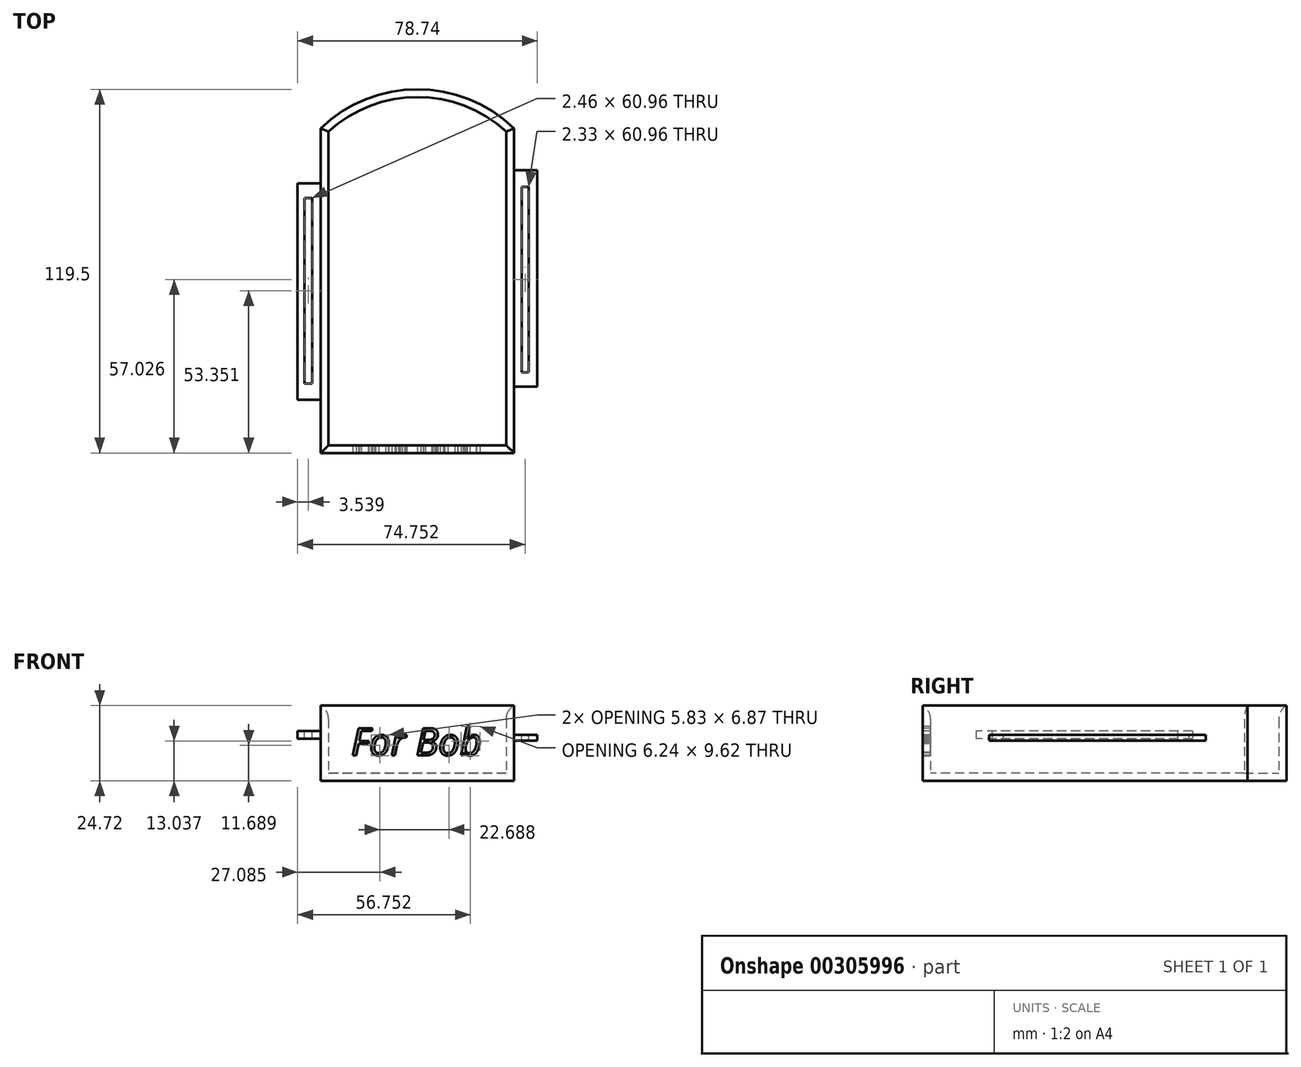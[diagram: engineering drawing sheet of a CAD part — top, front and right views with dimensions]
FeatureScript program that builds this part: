
annotation { "Feature Type Name" : "Feature", "Feature Type Description" : "" }
export const myFeature = defineFeature(function(context is Context, id is Id, definition is map)
    precondition{}
    {
        {
            var Q0;
            Q0=qCreatedBy(makeId("Top.planeOp"),FACE);
            var sketch = newSketch(context, id + "F0", { "sketchPlane" : qUnion([Q0])});
            skLineSegment(sketch, "E0", {"start": v(-35.9, 50.46) * mm, "end": v(-35.9, -56.22) * mm});
            skLineSegment(sketch, "E1", {"start": v(-35.9, -56.22) * mm, "end": v(27.6, -56.22) * mm});
            skLineSegment(sketch, "E2", {"start": v(27.6, -56.22) * mm, "end": v(27.6, 50.46) * mm});
            skArc(sketch, "E3", {"start": v(27.6, 50.46) * mm, "mid": v(-4.14, 63.28) * mm, "end": v(-35.9, 50.46) * mm});
            skSolve(sketch);
        }
        {
            var Q0;
            Q0 = qSketchRegion(id + "F0", true);
            extrude(context, id + "F1", {"entities" : qUnion([Q0]), "depth" : 25.4 * mm});
        }
        {
            var Q0;
            Q0=makeQuery(id+"F1.opExtrude","CAP_FACE",FACE,{"disambiguationData":[OSD([sQuery(id+"F0.wireOp",EDGE,"E0"),sQuery(id+"F0.wireOp",EDGE,"E1"),sQuery(id+"F0.wireOp",EDGE,"E2"),sQuery(id+"F0.wireOp",EDGE,"E3")])],"isStart":false});
            shell(context, id + "F2", {"entities" : qUnion([Q0]), "thickness" : 2.54 * mm});
        }
        {
            var Q0;
            {var subQ0=sQuery(id+"F0.wireOp",EDGE,"E3");Q0=makeQuery(id+"F2.opShell","OFFSET_EDGE",EDGE,{"disambiguationData":[OSD([subQ0]),TDD([makeQuery(id+"F1.opExtrude","CAP_EDGE",EDGE,{"disambiguationData":[OSD([subQ0])],"isStart":false})])]});}
            var Q1;
            {var subQ0=sQuery(id+"F0.wireOp",EDGE,"E0");Q1=makeQuery(id+"F2.opShell","OFFSET_EDGE",EDGE,{"disambiguationData":[OSD([subQ0]),TDD([makeQuery(id+"F1.opExtrude","CAP_EDGE",EDGE,{"disambiguationData":[OSD([subQ0])],"isStart":false})])]});}
            var Q2;
            {var subQ0=sQuery(id+"F0.wireOp",EDGE,"E2");Q2=makeQuery(id+"F2.opShell","OFFSET_EDGE",EDGE,{"disambiguationData":[OSD([subQ0]),TDD([makeQuery(id+"F1.opExtrude","CAP_EDGE",EDGE,{"disambiguationData":[OSD([subQ0])],"isStart":false})])]});}
            var Q3;
            {var subQ0=sQuery(id+"F0.wireOp",EDGE,"E1");Q3=makeQuery(id+"F2.opShell","OFFSET_EDGE",EDGE,{"disambiguationData":[OSD([subQ0]),TDD([makeQuery(id+"F1.opExtrude","CAP_EDGE",EDGE,{"disambiguationData":[OSD([subQ0])],"isStart":false})])]});}
            fillet(context, id + "F3", {"entities" : qUnion([Q0, Q1, Q2, Q3]), "radius" : 5.08 * mm, "tangentPropagation" : true, "allowEdgeOverflow" : false});
        }
        {
            var Q0;
            Q0=makeQuery(id+"F1.opExtrude","SWEPT_FACE",FACE,{"disambiguationData":[OSD([sQuery(id+"F0.wireOp",EDGE,"E1")])]});
            var sketch = newSketch(context, id + "F4", { "sketchPlane" : qUnion([Q0])});
            skText(sketch, "E4", { "text": "For Bob", "fontName": "OpenSans-Italic.ttf"});
            const initialGuessF4  = {"E4": [-0.02584, 0.00835, 1, 0, 0.009]};
            skSetInitialGuess(sketch, initialGuessF4);
            skSolve(sketch);
        }
        {
            var Q0;
            Q0 = qSketchRegion(id + "F4", true);
            extrude(context, id + "F5", {"entities" : qUnion([Q0]), "operationType" : NewBodyOperationType.REMOVE, "oppositeDirection" : true, "depth" : 12.7 * mm});
        }
        {
            var Q0;
            Q0=makeQuery(id+"F1.opExtrude","SWEPT_FACE",FACE,{"disambiguationData":[OSD([sQuery(id+"F0.wireOp",EDGE,"E2")])]});
            var sketch = newSketch(context, id + "F6", { "sketchPlane" : qUnion([Q0])});
            skLineSegment(sketch, "E5.bottom", {"start": v(-34.4, 15.16) * mm, "end": v(36.73, 15.16) * mm});
            skLineSegment(sketch, "E5.top", {"start": v(-34.4, 13.18) * mm, "end": v(36.73, 13.18) * mm});
            skLineSegment(sketch, "E5.left", {"start": v(-34.4, 15.16) * mm, "end": v(-34.4, 13.18) * mm});
            skLineSegment(sketch, "E5.right", {"start": v(36.73, 15.16) * mm, "end": v(36.73, 13.18) * mm});
            skSolve(sketch);
        }
        {
            var Q0;
            Q0 = qSketchRegion(id + "F6", true);
            extrude(context, id + "F7", {"entities" : qUnion([Q0]), "operationType" : NewBodyOperationType.ADD, "depth" : 7.62 * mm});
        }
        {
            var Q0;
            Q0=makeQuery(id+"F7.opExtrude","SWEPT_FACE",FACE,{"disambiguationData":[OSD([sQuery(id+"F6.wireOp",EDGE,"E5.bottom")])]});
            var sketch = newSketch(context, id + "F8", { "sketchPlane" : qUnion([Q0])});
            skLineSegment(sketch, "E6.bottom", {"start": v(30.08, -29.67) * mm, "end": v(32.4, -29.67) * mm});
            skLineSegment(sketch, "E6.top", {"start": v(30.08, 31.29) * mm, "end": v(32.4, 31.29) * mm});
            skLineSegment(sketch, "E6.left", {"start": v(30.08, -29.67) * mm, "end": v(30.08, 31.29) * mm});
            skLineSegment(sketch, "E6.right", {"start": v(32.4, -29.67) * mm, "end": v(32.4, 31.29) * mm});
            skSolve(sketch);
        }
        {
            var Q0;
            Q0 = qSketchRegion(id + "F8", true);
            extrude(context, id + "F9", {"entities" : qUnion([Q0]), "operationType" : NewBodyOperationType.REMOVE, "oppositeDirection" : true, "depth" : 25.4 * mm});
        }
        {
            var Q0;
            Q0=makeQuery(id+"F1.opExtrude","SWEPT_FACE",FACE,{"disambiguationData":[OSD([sQuery(id+"F0.wireOp",EDGE,"E0")])]});
            var sketch = newSketch(context, id + "F10", { "sketchPlane" : qUnion([Q0])});
            skLineSegment(sketch, "E7.bottom", {"start": v(-32.36, 16.41) * mm, "end": v(38.76, 16.41) * mm});
            skLineSegment(sketch, "E7.top", {"start": v(-32.36, 13.81) * mm, "end": v(38.76, 13.81) * mm});
            skLineSegment(sketch, "E7.left", {"start": v(-32.36, 16.41) * mm, "end": v(-32.36, 13.81) * mm});
            skLineSegment(sketch, "E7.right", {"start": v(38.76, 16.41) * mm, "end": v(38.76, 13.81) * mm});
            skSolve(sketch);
        }
        {
            var Q0;
            Q0 = qSketchRegion(id + "F10", true);
            extrude(context, id + "F11", {"entities" : qUnion([Q0]), "operationType" : NewBodyOperationType.ADD, "depth" : 7.62 * mm});
        }
        {
            var Q0;
            Q0=makeQuery(id+"F11.opExtrude","SWEPT_FACE",FACE,{"disambiguationData":[OSD([sQuery(id+"F10.wireOp",EDGE,"E7.bottom")])]});
            var sketch = newSketch(context, id + "F12", { "sketchPlane" : qUnion([Q0])});
            skLineSegment(sketch, "E8.bottom", {"start": v(-38.74, 27.61) * mm, "end": v(-41.2, 27.61) * mm});
            skLineSegment(sketch, "E8.top", {"start": v(-38.74, -33.35) * mm, "end": v(-41.2, -33.35) * mm});
            skLineSegment(sketch, "E8.left", {"start": v(-38.74, 27.61) * mm, "end": v(-38.74, -33.35) * mm});
            skLineSegment(sketch, "E8.right", {"start": v(-41.2, 27.61) * mm, "end": v(-41.2, -33.35) * mm});
            skSolve(sketch);
        }
        {
            var Q0;
            Q0 = qSketchRegion(id + "F12", true);
            extrude(context, id + "F13", {"entities" : qUnion([Q0]), "operationType" : NewBodyOperationType.REMOVE, "oppositeDirection" : true, "depth" : 25.4 * mm});
        }
    });
